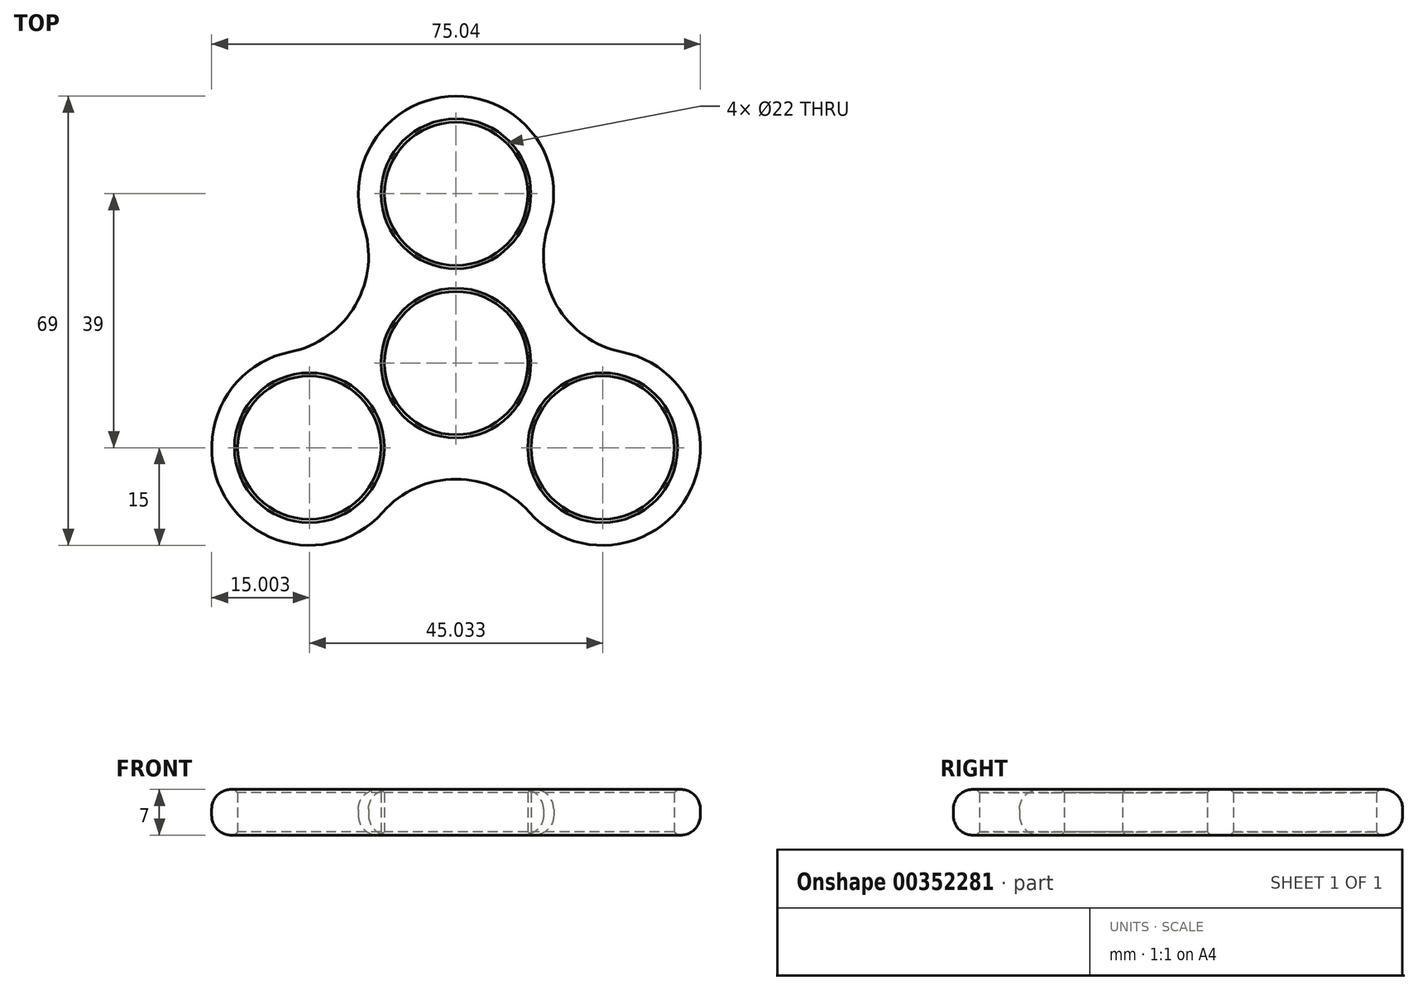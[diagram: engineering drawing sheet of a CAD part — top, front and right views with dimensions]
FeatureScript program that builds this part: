
annotation { "Feature Type Name" : "Feature", "Feature Type Description" : "" }
export const myFeature = defineFeature(function(context is Context, id is Id, definition is map)
    precondition{}
    {
        {
            var Q0;
            Q0=qCreatedBy(makeId("Top.planeOp"),FACE);
            var sketch = newSketch(context, id + "F0", { "sketchPlane" : qUnion([Q0])});
            skCircle(sketch, "E0", {"center": v(0, 0) * mm, "radius": 11 * mm});
            skLineSegment(sketch, "E1", {"start": v(0, 0) * mm, "end": v(0, 26) * mm, "construction": true});
            skCircle(sketch, "E2", {"center": v(0, 26) * mm, "radius": 11 * mm});
            skCircle(sketch, "E3.1.0", {"center": v(-22.52, -13) * mm, "radius": 11 * mm});
            skCircle(sketch, "E3.2.0", {"center": v(22.52, -13) * mm, "radius": 11 * mm});
            skArc(sketch, "E4", {"start": v(-14.21, 21.2) * mm, "mid": v(0, 41) * mm, "end": v(14.21, 21.2) * mm});
            skArc(sketch, "E5.1.0", {"start": v(-11.26, -22.91) * mm, "mid": v(-35.5, -20.5) * mm, "end": v(-25.47, 1.7) * mm});
            skArc(sketch, "E5.2.0", {"start": v(25.47, 1.7) * mm, "mid": v(35.5, -20.5) * mm, "end": v(11.26, -22.91) * mm});
            skArc(sketch, "E6", {"start": v(14.21, 21.2) * mm, "mid": v(15.44, 8.91) * mm, "end": v(25.47, 1.7) * mm});
            skArc(sketch, "E7.1.0", {"start": v(-25.47, 1.7) * mm, "mid": v(-15.44, 8.91) * mm, "end": v(-14.21, 21.2) * mm});
            skArc(sketch, "E7.2.0", {"start": v(11.26, -22.91) * mm, "mid": v(0, -17.82) * mm, "end": v(-11.26, -22.91) * mm});
            skSolve(sketch);
        }
        {
            var Q0;
            Q0=makeQuery(id+"F0.imprint","IMPRINT",FACE,{"disambiguationData":[TD([[makeQuery(id+"F0.imprint","IMPRINT",EDGE,{"derivedFrom":sQuery(id+"F0.wireOp",EDGE,"E0")}),-1.0]])]});
            extrude(context, id + "F1", {"entities" : qUnion([Q0]), "depth" : 7 * mm});
        }
        {
            var Q0;
            Q0=makeQuery(id+"F1.opExtrude","CAP_EDGE",EDGE,{"disambiguationData":[OSD([sQuery(id+"F0.wireOp",EDGE,"E4")])],"isStart":false});
            var Q1;
            Q1=makeQuery(id+"F1.opExtrude","CAP_EDGE",EDGE,{"disambiguationData":[OSD([sQuery(id+"F0.wireOp",EDGE,"E4")])],"isStart":true});
            fillet(context, id + "F2", {"entities" : qUnion([Q0, Q1]), "radius" : 3 * mm, "tangentPropagation" : true, "allowEdgeOverflow" : false});
        }
        {
            var Q0;
            Q0=makeQuery(id+"F1.opExtrude","CAP_FACE",FACE,{"disambiguationData":[OSD([sQuery(id+"F0.wireOp",EDGE,"E0"),sQuery(id+"F0.wireOp",EDGE,"E2"),sQuery(id+"F0.wireOp",EDGE,"E3.1.0"),sQuery(id+"F0.wireOp",EDGE,"E3.2.0"),sQuery(id+"F0.wireOp",EDGE,"E4"),sQuery(id+"F0.wireOp",EDGE,"E5.1.0"),sQuery(id+"F0.wireOp",EDGE,"E5.2.0"),sQuery(id+"F0.wireOp",EDGE,"E6"),sQuery(id+"F0.wireOp",EDGE,"E7.1.0"),sQuery(id+"F0.wireOp",EDGE,"E7.2.0")])],"isStart":true});
            var Q1;
            Q1=makeQuery(id+"F1.opExtrude","CAP_FACE",FACE,{"disambiguationData":[OSD([sQuery(id+"F0.wireOp",EDGE,"E0"),sQuery(id+"F0.wireOp",EDGE,"E2"),sQuery(id+"F0.wireOp",EDGE,"E3.1.0"),sQuery(id+"F0.wireOp",EDGE,"E3.2.0"),sQuery(id+"F0.wireOp",EDGE,"E4"),sQuery(id+"F0.wireOp",EDGE,"E5.1.0"),sQuery(id+"F0.wireOp",EDGE,"E5.2.0"),sQuery(id+"F0.wireOp",EDGE,"E6"),sQuery(id+"F0.wireOp",EDGE,"E7.1.0"),sQuery(id+"F0.wireOp",EDGE,"E7.2.0")])],"isStart":false});
            chamfer(context, id + "F3", {"entities" : qUnion([Q0, Q1]), "width" : .5 * mm, "tangentPropagation" : true});
        }
    });
